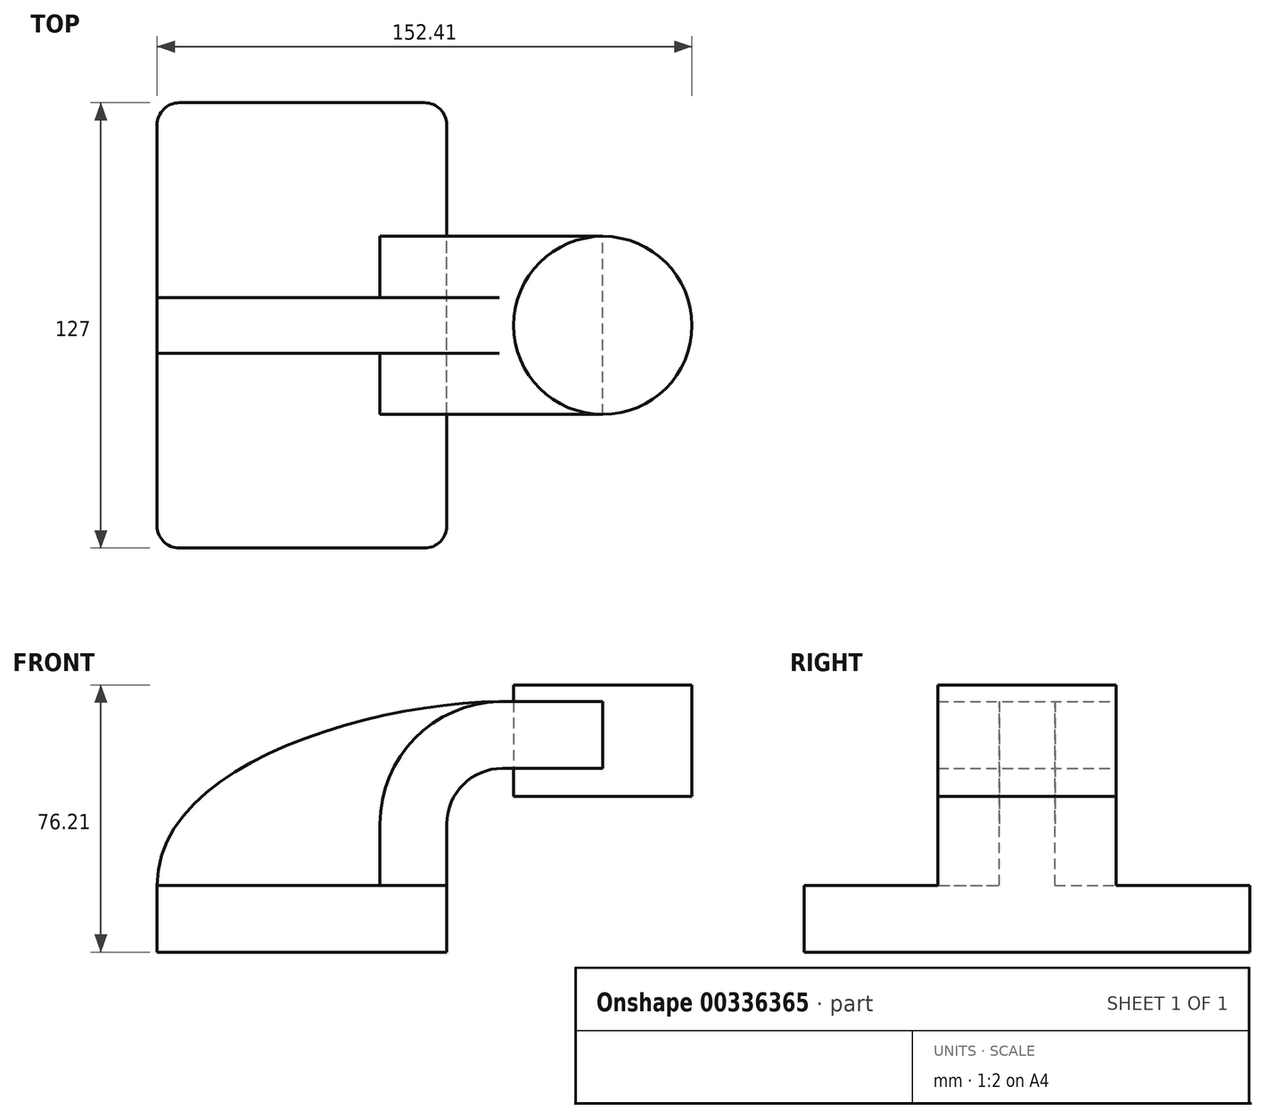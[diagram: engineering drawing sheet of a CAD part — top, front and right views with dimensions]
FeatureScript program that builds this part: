
annotation { "Feature Type Name" : "Feature", "Feature Type Description" : "" }
export const myFeature = defineFeature(function(context is Context, id is Id, definition is map)
    precondition{}
    {
        {
            var Q0;
            Q0=qCreatedBy(makeId("Front.planeOp"),FACE);
            var sketch = newSketch(context, id + "F0", { "sketchPlane" : qUnion([Q0])});
            skLineSegment(sketch, "E0.bottom", {"start": v(-41.28, -9.53) * mm, "end": v(41.28, -9.53) * mm});
            skLineSegment(sketch, "E0.top", {"start": v(-41.28, 9.53) * mm, "end": v(41.28, 9.53) * mm});
            skLineSegment(sketch, "E0.left", {"start": v(-41.28, -9.53) * mm, "end": v(-41.28, 9.53) * mm});
            skLineSegment(sketch, "E0.right", {"start": v(41.28, -9.53) * mm, "end": v(41.28, 9.53) * mm});
            skPoint(sketch, "E0.middle", {"position": v(0, 0) * mm});
            skLineSegment(sketch, "E1.bottom", {"start": v(111.13, 34.93) * mm, "end": v(60.33, 34.93) * mm});
            skLineSegment(sketch, "E1.top", {"start": v(111.13, 66.68) * mm, "end": v(60.33, 66.67) * mm});
            skLineSegment(sketch, "E1.left", {"start": v(111.13, 34.93) * mm, "end": v(111.13, 66.68) * mm});
            skLineSegment(sketch, "E1.right", {"start": v(60.33, 34.93) * mm, "end": v(60.33, 66.68) * mm});
            skPoint(sketch, "E1.middle", {"position": v(85.73, 50.8) * mm});
            skLineSegment(sketch, "E2", {"start": v(41.28, 9.52) * mm, "end": v(41.28, 27) * mm});
            skArc(sketch, "E3", {"start": v(41.27, 27) * mm, "mid": v(45.92, 38.23) * mm, "end": v(57.15, 42.88) * mm});
            skLineSegment(sketch, "E4", {"start": v(57.15, 42.88) * mm, "end": v(85.72, 42.88) * mm});
            skLineSegment(sketch, "E5.0", {"start": v(57.15, 61.93) * mm, "end": v(85.72, 61.93) * mm});
            skArc(sketch, "E5.1", {"start": v(22.22, 27) * mm, "mid": v(32.45, 51.7) * mm, "end": v(57.15, 61.93) * mm});
            skLineSegment(sketch, "E5.2", {"start": v(22.22, 9.52) * mm, "end": v(22.22, 27) * mm});
            skLineSegment(sketch, "E6", {"start": v(85.73, 34.93) * mm, "end": v(85.73, 66.68) * mm});
            skFitSpline(sketch, "E7", {"points": [v(-41.28, 9.53) * mm, v(57.15, 61.93) * mm], "startDerivative": vector(-0.7, 102.38) * mm, "endDerivative": vector(115.9, 1.07) * mm});
            skSolve(sketch);
        }
        {
            var Q0;
            Q0=makeQuery(id+"F0.imprint","IMPRINT",FACE,{"disambiguationData":[TD([[makeQuery(id+"F0.imprint","IMPRINT",EDGE,{"derivedFrom":sQuery(id+"F0.wireOp",EDGE,"E0.bottom")}),1.0]])]});
            extrude(context, id + "F1", {"entities" : qUnion([Q0]), "endBound" : BoundingType.SYMMETRIC, "depth" : 127 * mm});
        }
        {
            var Q0;
            {var subQ1=sQuery(id+"F0.wireOp",EDGE,"E2");Q0=makeQuery(id+"F0.imprint","IMPRINT",FACE,{"disambiguationData":[TD([[makeQuery(id+"F0.imprint","IMPRINT",EDGE,{"derivedFrom":subQ1}),1.0]])]});}
            var Q1;
            {var subQ0=sQuery(id+"F0.wireOp",EDGE,"E4");var subQ1=sQuery(id+"F0.wireOp",EDGE,"E1.right");var subQ2=makeQuery(id+"F0.imprint","INTERSECT",VERTEX,{"derivedFrom":[subQ1,subQ0]});Q1=makeQuery(id+"F0.imprint","IMPRINT",FACE,{"disambiguationData":[TD([[makeQuery(id+"F0.imprint","IMPRINT",EDGE,{"disambiguationData":[TD([[subQ2,-1.0]])],"derivedFrom":subQ1}),-1.0]])]});}
            extrude(context, id + "F2", {"entities" : qUnion([Q0, Q1]), "operationType" : NewBodyOperationType.ADD, "endBound" : BoundingType.SYMMETRIC, "depth" : 50.8 * mm});
        }
        {
            var Q0;
            {var subQ3=sQuery(id+"F0.wireOp",EDGE,"E5.2");Q0=makeQuery(id+"F0.imprint","IMPRINT",FACE,{"disambiguationData":[TD([[makeQuery(id+"F0.imprint","IMPRINT",EDGE,{"derivedFrom":subQ3}),1.0]])]});}
            extrude(context, id + "F3", {"entities" : qUnion([Q0]), "operationType" : NewBodyOperationType.ADD, "endBound" : BoundingType.SYMMETRIC, "depth" : 15.88 * mm});
        }
        {
            var Q0;
            {var subQ0=sQuery(id+"F0.wireOp",EDGE,"E1.left");Q0=makeQuery(id+"F0.imprint","IMPRINT",FACE,{"disambiguationData":[TD([[makeQuery(id+"F0.imprint","IMPRINT",EDGE,{"derivedFrom":subQ0}),1.0]])]});}
            var Q1;
            Q1=sQuery(id+"F0.wireOp",EDGE,"E6");
            revolve(context, id + "F4", {"entities" : qUnion([Q0]), "axis" : qUnion([Q1]), "revolveType" : RevolveType.FULL});
        }
        {
            var Q0;
            Q0=makeQuery(id+"F1.opExtrude","CAP_EDGE",EDGE,{"disambiguationData":[OSD([sQuery(id+"F0.wireOp",EDGE,"E0.left")])],"isStart":false});
            var Q1;
            Q1=makeQuery(id+"F1.opExtrude","CAP_EDGE",EDGE,{"disambiguationData":[OSD([sQuery(id+"F0.wireOp",EDGE,"E0.right")])],"isStart":false});
            var Q2;
            Q2=makeQuery(id+"F1.opExtrude","CAP_EDGE",EDGE,{"disambiguationData":[OSD([sQuery(id+"F0.wireOp",EDGE,"E0.right")])],"isStart":true});
            var Q3;
            Q3=makeQuery(id+"F1.opExtrude","CAP_EDGE",EDGE,{"disambiguationData":[OSD([sQuery(id+"F0.wireOp",EDGE,"E0.left")])],"isStart":true});
            fillet(context, id + "F5", {"entities" : qUnion([Q0, Q1, Q2, Q3]), "radius" : 6.35 * mm, "tangentPropagation" : true, "allowEdgeOverflow" : false});
        }
    });
